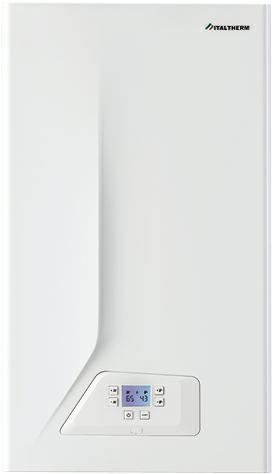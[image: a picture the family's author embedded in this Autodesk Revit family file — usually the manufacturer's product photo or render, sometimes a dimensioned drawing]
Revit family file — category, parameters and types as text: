
# Revit family: City Class H K
name_source: partatom
category: Attrezzatura meccanica
units: mm (PartAtom-declared; Revit-internal decimal feet)

## family parameters
Classificazione = Nessuno
Condiviso = No
Host = Muro
Mantieni orientamento annotazione = No
Punto di calcolo locali = No
Quota connettore circolare = Usa diametro
Sempre verticale = Sì
Taglio con vuoti quando caricato = No
Tipo di parte = Normale

## types (3) — shared parameters
Combustion air inlet - separate system = 80 mm  [stored 0.262467 ft]
Date of publishing = 22/07/2019
Depth = 324 mm  [stored 1.06299 ft]
Design country = Italy
Domestic Cold Water Diameter = 21 mm  [stored 0.0688976 ft]
Domestic Hot Water Diameter = 21 mm  [stored 0.0688976 ft]
Energetic efficiency (92/42/CEE) = n.d.
Flue outlet = 100 mm  [stored 0.328084 ft]
Gas Inlet Diameter = 26 mm
Height = 700 mm  [stored 2.29659 ft]
Hydronic Return Diameter = 26 mm
Hydronic Supply Diameter = 26 mm
IFC Classification = Boiler
Immagine tipo = city class.jpg
Manufacturer country = Italy
Manufacturer name = Italtherm S.p.A.
Material main = Metal
Material secondary = Plastic
NBS reference Description = Boilers
Omniclass Description = Condensing boilers
Power supply | Frequency (Hz) = 50
Power supply | Phase = 1
Power supply | Voltage (V) = 230 V
Product family = Heating
Product group = Thermal unit
Siphon with condensate drain = 25 mm  [stored 0.082021 ft]
Uniclass 2015 Name = Boilers
Width = 400 mm  [stored 1.31234 ft]
zero-valued in all types: Edition number, Prospetto di default

## per-type parameters (varying)
| type | Efficiency 30% | Maximum heat output 50/30°C | Maximum heat output 80/60°C | Maximum heating heat input | Minimum heat output 50/30°C | Minimum heat output 80/60°C | Nominal efficiency 50/30°C | Nominal efficiency 80/60°C | Power consumption (W) | URL | URL ENG | Weight |
| City Class H 25 K | 106.2 | 22.1 | 20.3 | 21 | 2.7 | 2.4 | 105.8 | 95.9 | 73 | www.italtherm.it/g/caldaia-a-gas-da-interno/caldaia-a-condensazione/city-class-k/25-kw | en.italtherm.it/g/wall-hung-condensing-boilers/gas-boiler/city-class-k/25-kw | 28.50 kg |
| City Class H 30 K | 106.0 | 26.1 | 24 | 25 | 2.7 | 2.4 | 105.4 | 95.9 | 85 | www.italtherm.it/g/caldaia-a-gas-da-interno/caldaia-a-condensazione/city-class-k/30-kw | en.italtherm.it/g/wall-hung-condensing-boilers/gas-boiler/city-class-k/30-kw | 28.70 kg |
| City Class H 35 K | 106.9 | 29 | 26.3 | 28 | 3.7 | 3.2 | 105.1 | 95.2 | 86 | www.italtherm.it/g/caldaia-a-gas-da-interno/caldaia-a-condensazione/city-class-k/35-kw | en.italtherm.it/g/wall-hung-condensing-boilers/gas-boiler/city-class-k/35-kw | 34.00 kg |

note: [stored X ft] marks values corroborated as IEEE doubles in the binary element streams (Revit-internal decimal feet)
